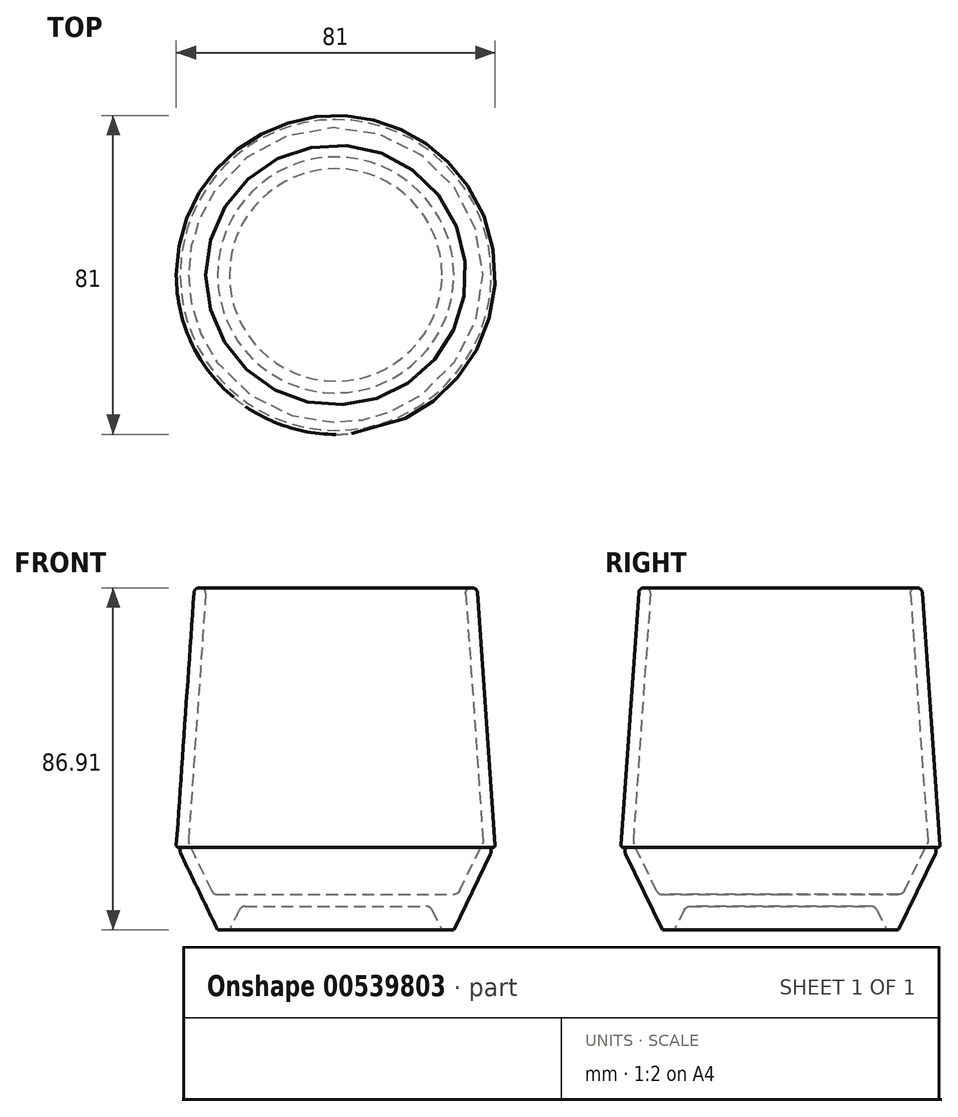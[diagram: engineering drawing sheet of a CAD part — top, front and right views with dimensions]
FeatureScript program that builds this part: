
annotation { "Feature Type Name" : "Feature", "Feature Type Description" : "" }
export const myFeature = defineFeature(function(context is Context, id is Id, definition is map)
    precondition{}
    {
        {
            var Q0;
            Q0=qCreatedBy(makeId("Front.planeOp"),FACE);
            var sketch = newSketch(context, id + "F0", { "sketchPlane" : qUnion([Q0])});
            skLineSegment(sketch, "E0", {"start": v(0, 6) * mm, "end": v(23, 6) * mm});
            skLineSegment(sketch, "E1", {"start": v(24.45, 5.1) * mm, "end": v(27, 0) * mm});
            skLineSegment(sketch, "E2", {"start": v(27, 0) * mm, "end": v(30, 0) * mm});
            skLineSegment(sketch, "E3", {"start": v(30, 0) * mm, "end": v(39.34, 19.29) * mm});
            skLineSegment(sketch, "E4", {"start": v(40.5, 21.53) * mm, "end": v(36.01, 85.7) * mm});
            skLineSegment(sketch, "E5", {"start": v(34.63, 86.9) * mm, "end": v(34.23, 86.88) * mm});
            skLineSegment(sketch, "E6", {"start": v(33.02, 85.5) * mm, "end": v(37.41, 22.7) * mm});
            skLineSegment(sketch, "E7", {"start": v(37.25, 21.87) * mm, "end": v(31.47, 9.92) * mm});
            skLineSegment(sketch, "E8", {"start": v(30, 9) * mm, "end": v(0, 9) * mm});
            skLineSegment(sketch, "E9", {"start": v(0, 9) * mm, "end": v(0, 6) * mm});
            skPoint(sketch, "E10.visualSharp", {"position": v(24, 6) * mm});
            skArc(sketch, "E10.filletArc", {"start": v(24.45, 5.1) * mm, "mid": v(23.85, 5.76) * mm, "end": v(23, 6) * mm});
            skPoint(sketch, "E11.visualSharp", {"position": v(31.02, 9) * mm});
            skArc(sketch, "E11.filletArc", {"start": v(30, 9) * mm, "mid": v(30.87, 9.25) * mm, "end": v(31.47, 9.92) * mm});
            skPoint(sketch, "E12.visualSharp", {"position": v(37.44, 22.26) * mm});
            skArc(sketch, "E12.filletArc", {"start": v(37.25, 21.87) * mm, "mid": v(37.39, 22.27) * mm, "end": v(37.41, 22.7) * mm});
            skPoint(sketch, "E13.visualSharp", {"position": v(39.01, 18.62) * mm});
            skArc(sketch, "E13.filletArc", {"start": v(39.34, 19.29) * mm, "mid": v(39.46, 19.64) * mm, "end": v(39.5, 20) * mm});
            skPoint(sketch, "E14.visualSharp", {"position": v(35.92, 87) * mm});
            skArc(sketch, "E14.filletArc", {"start": v(36.01, 85.7) * mm, "mid": v(35.57, 86.6) * mm, "end": v(34.63, 86.9) * mm});
            skPoint(sketch, "E15.visualSharp", {"position": v(32.93, 86.8) * mm});
            skArc(sketch, "E15.filletArc", {"start": v(34.23, 86.88) * mm, "mid": v(33.34, 86.44) * mm, "end": v(33.02, 85.5) * mm});
            skLineSegment(sketch, "E16", {"start": v(40.5, 21.53) * mm, "end": v(40.5, 87) * mm, "construction": true});
            skLineSegment(sketch, "E17", {"start": v(0, 0) * mm, "end": v(0, 85.7) * mm, "construction": true});
            skLineSegment(sketch, "E18", {"start": v(39.5, 20) * mm, "end": v(39.5, 20.5) * mm});
            skArc(sketch, "E19", {"start": v(40, 21) * mm, "mid": v(40.37, 21.16) * mm, "end": v(40.5, 21.53) * mm});
            skLineSegment(sketch, "E20", {"start": v(40, 21) * mm, "end": v(40, 21) * mm});
            skArc(sketch, "E21", {"start": v(40, 21) * mm, "mid": v(39.65, 20.85) * mm, "end": v(39.5, 20.5) * mm});
            skSolve(sketch);
        }
        {
            var Q0;
            Q0=qSketchRegion(id+"F0",true);
            var Q1;
            Q1=sQuery(id+"F0.wireOp",EDGE,"E17");
            revolve(context, id + "F1", {"entities" : qUnion([Q0]), "axis" : qUnion([Q1]), "revolveType" : RevolveType.FULL});
        }
    });
